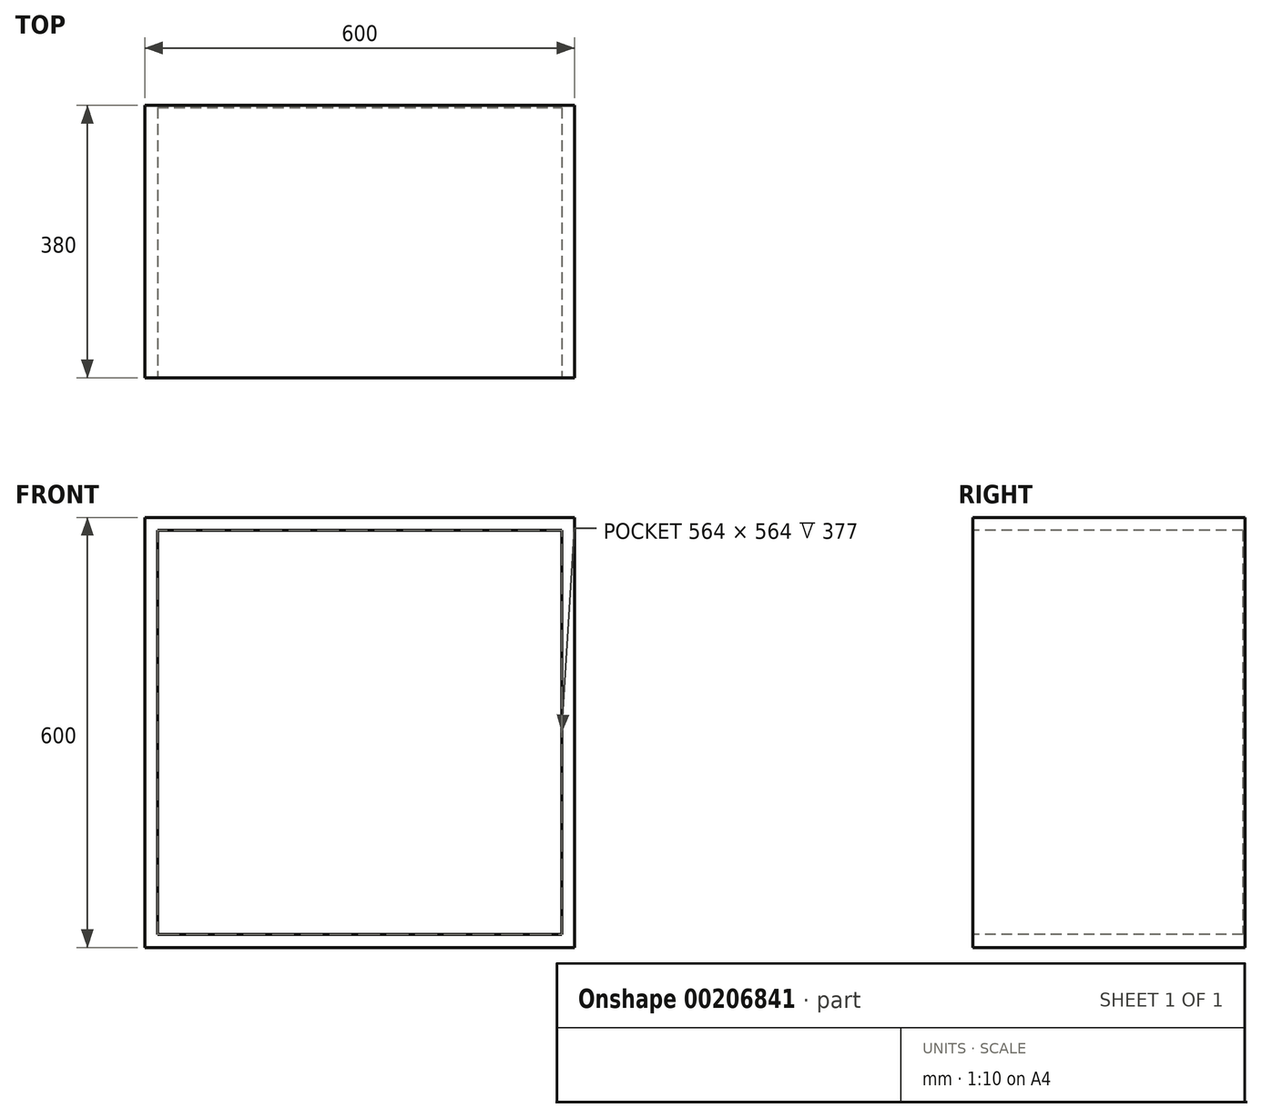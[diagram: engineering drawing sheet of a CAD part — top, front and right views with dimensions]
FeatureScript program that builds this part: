
annotation { "Feature Type Name" : "Feature", "Feature Type Description" : "" }
export const myFeature = defineFeature(function(context is Context, id is Id, definition is map)
    precondition{}
    {
        {
            var Q0;
            Q0=qCreatedBy(makeId("Top.planeOp"),FACE);
            var sketch = newSketch(context, id + "F0", { "sketchPlane" : qUnion([Q0])});
            skLineSegment(sketch, "E0.bottom", {"start": v(-518.83, 334.1) * mm, "end": v(81.17, 334.1) * mm});
            skLineSegment(sketch, "E0.top", {"start": v(-518.83, -45.9) * mm, "end": v(-500.83, -45.9) * mm});
            skLineSegment(sketch, "E0.left", {"start": v(-518.83, 334.1) * mm, "end": v(-518.83, -45.9) * mm});
            skLineSegment(sketch, "E0.right", {"start": v(81.17, 334.1) * mm, "end": v(81.17, -45.9) * mm});
            skLineSegment(sketch, "E1.bottom", {"start": v(-500.83, 331.1) * mm, "end": v(63.17, 331.1) * mm});
            skLineSegment(sketch, "E1.left", {"start": v(-500.83, 331.1) * mm, "end": v(-500.83, -45.9) * mm});
            skLineSegment(sketch, "E1.right", {"start": v(63.17, 331.1) * mm, "end": v(63.17, -45.9) * mm});
            skLineSegment(sketch, "E2.trimOffspring", {"start": v(63.17, -45.9) * mm, "end": v(81.17, -45.9) * mm});
            skSolve(sketch);
        }
        {
            var Q0;
            Q0=qCreatedBy(makeId("Top.planeOp"),FACE);
            var sketch = newSketch(context, id + "F1", { "sketchPlane" : qUnion([Q0])});
            skPoint(sketch, "E3.0", {"position": v(-518.83, 334.1) * mm});
            skLineSegment(sketch, "E4.0", {"start": v(-518.83, 334.1) * mm, "end": v(-518.83, -45.9) * mm});
            skLineSegment(sketch, "E5.0", {"start": v(-518.83, 334.1) * mm, "end": v(81.17, 334.1) * mm});
            skLineSegment(sketch, "E6.0", {"start": v(81.17, 334.1) * mm, "end": v(81.17, -45.9) * mm});
            skLineSegment(sketch, "E7", {"start": v(-518.83, -45.9) * mm, "end": v(81.17, -45.9) * mm});
            skSolve(sketch);
        }
        {
            var Q0;
            Q0=qSketchRegion(id+"F0",true);
            extrude(context, id + "F2", {"entities" : qUnion([Q0]), "depth" : 600 * mm});
        }
        {
            var Q0;
            Q0=qSketchRegion(id+"F1",true);
            extrude(context, id + "F3", {"entities" : qUnion([Q0]), "operationType" : NewBodyOperationType.ADD, "depth" : 18 * mm});
        }
        {
            var Q0;
            Q0=makeQuery(id+"F2.opExtrude","CAP_FACE",FACE,{"disambiguationData":[OSD([sQuery(id+"F0.wireOp",EDGE,"E0.bottom"),sQuery(id+"F0.wireOp",EDGE,"E0.top"),sQuery(id+"F0.wireOp",EDGE,"E0.left"),sQuery(id+"F0.wireOp",EDGE,"E0.right"),sQuery(id+"F0.wireOp",EDGE,"E1.bottom"),sQuery(id+"F0.wireOp",EDGE,"E1.left"),sQuery(id+"F0.wireOp",EDGE,"E1.right"),sQuery(id+"F0.wireOp",EDGE,"E2.trimOffspring")])],"isStart":false});
            var sketch = newSketch(context, id + "F4", { "sketchPlane" : qUnion([Q0])});
            skLineSegment(sketch, "E8.0.0", {"start": v(81.17, -45.9) * mm, "end": v(-518.83, -45.9) * mm});
            skLineSegment(sketch, "E8.0.1", {"start": v(-518.83, -45.9) * mm, "end": v(-518.83, 334.1) * mm});
            skLineSegment(sketch, "E8.0.2", {"start": v(-518.83, 334.1) * mm, "end": v(81.17, 334.1) * mm});
            skLineSegment(sketch, "E8.0.3", {"start": v(81.17, 334.1) * mm, "end": v(81.17, -45.9) * mm});
            skSolve(sketch);
        }
        {
            var Q0;
            Q0=makeQuery(id+"F4.imprint","IMPRINT",FACE,{"disambiguationData":[TD([[makeQuery(id+"F4.imprint","IMPRINT",EDGE,{"derivedFrom":makeQuery(id+"F2.opExtrude","CAP_EDGE",EDGE,{"disambiguationData":[OSD([sQuery(id+"F0.wireOp",EDGE,"E1.bottom")])],"isStart":false})}),-1.0]])]});
            extrude(context, id + "F5", {"entities" : qUnion([Q0]), "operationType" : NewBodyOperationType.ADD, "oppositeDirection" : true, "depth" : 18 * mm});
        }
    });
